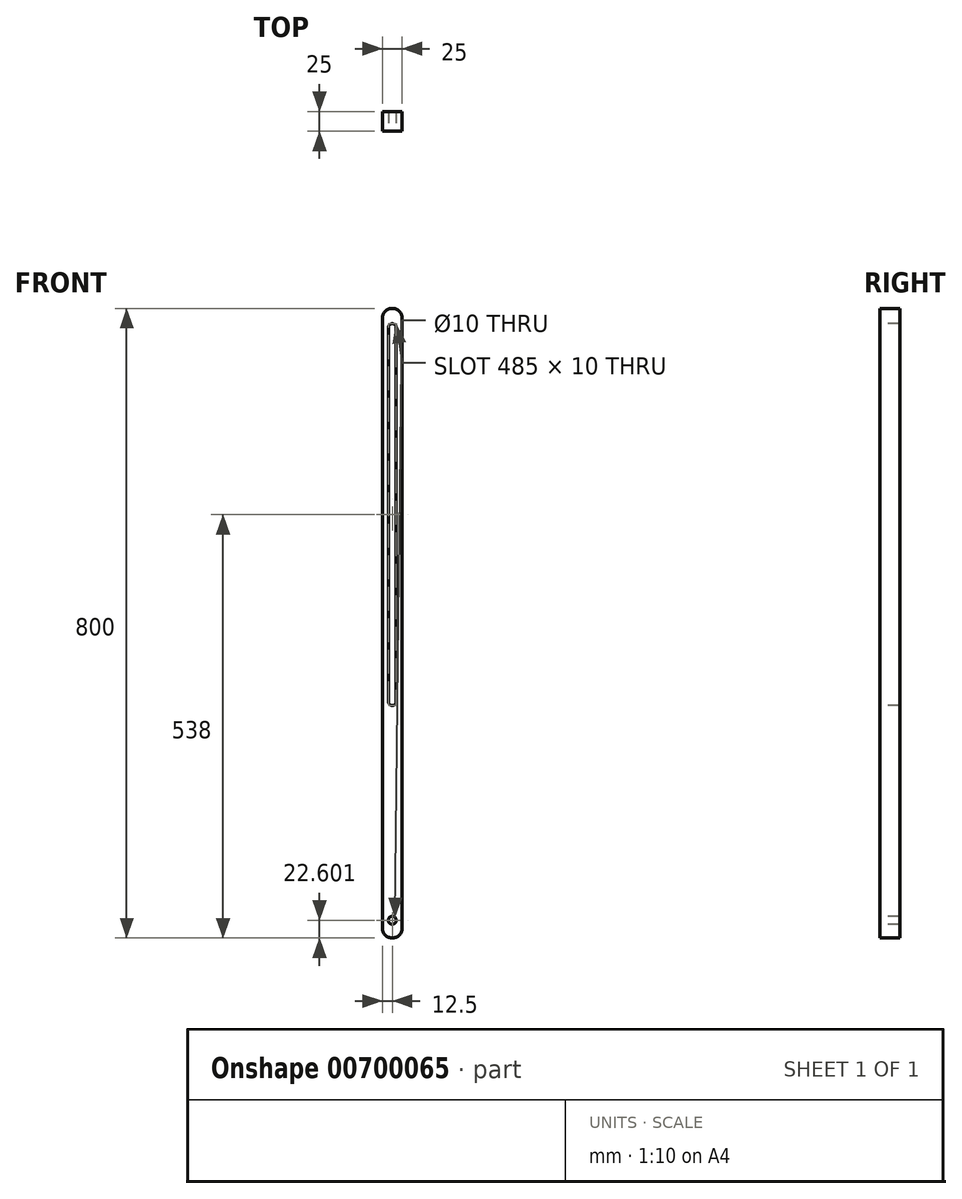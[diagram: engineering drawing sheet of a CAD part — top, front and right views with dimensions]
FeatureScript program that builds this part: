
annotation { "Feature Type Name" : "Feature", "Feature Type Description" : "" }
export const myFeature = defineFeature(function(context is Context, id is Id, definition is map)
    precondition{}
    {
        {
            var Q0;
            Q0=qCreatedBy(makeId("Front.planeOp"),FACE);
            var sketch = newSketch(context, id + "F0", { "sketchPlane" : qUnion([Q0])});
            skLineSegment(sketch, "E0.bottom", {"start": v(-12.5, 400) * mm, "end": v(12.5, 400) * mm});
            skLineSegment(sketch, "E0.top", {"start": v(-12.5, -400) * mm, "end": v(12.5, -400) * mm});
            skLineSegment(sketch, "E0.left", {"start": v(-12.5, 400) * mm, "end": v(-12.5, -400) * mm});
            skLineSegment(sketch, "E0.right", {"start": v(12.5, 400) * mm, "end": v(12.5, -400) * mm});
            skPoint(sketch, "E0.middle", {"position": v(0, 0) * mm});
            skSolve(sketch);
        }
        {
            var Q0;
            Q0=makeQuery(id+"F0.imprint","IMPRINT",FACE,{"disambiguationData":[TD([[makeQuery(id+"F0.imprint","IMPRINT",EDGE,{"derivedFrom":sQuery(id+"F0.wireOp",EDGE,"E0.bottom")}),-1.0]])]});
            extrude(context, id + "F1", {"entities" : qUnion([Q0]), "depth" : 25 * mm, "offsetDistance" : 25.4 * mm});
        }
        {
            var Q0;
            Q0=makeQuery(id+"F1.opExtrude","CAP_FACE",FACE,{"disambiguationData":[OSD([sQuery(id+"F0.wireOp",EDGE,"E0.bottom"),sQuery(id+"F0.wireOp",EDGE,"E0.top"),sQuery(id+"F0.wireOp",EDGE,"E0.left"),sQuery(id+"F0.wireOp",EDGE,"E0.right")])],"isStart":false});
            var sketch = newSketch(context, id + "F2", { "sketchPlane" : qUnion([Q0])});
            skLineSegment(sketch, "E1.bottom", {"start": v(5, 375.5) * mm, "end": v(-5, 375.5) * mm});
            skLineSegment(sketch, "E1.top", {"start": v(5, -99.5) * mm, "end": v(-5, -99.5) * mm});
            skLineSegment(sketch, "E1.left", {"start": v(5, 375.5) * mm, "end": v(5, -99.5) * mm});
            skLineSegment(sketch, "E1.right", {"start": v(-5, 375.5) * mm, "end": v(-5, -99.5) * mm});
            skPoint(sketch, "E1.middle", {"position": v(0, 138) * mm});
            skSolve(sketch);
        }
        {
            var Q0;
            Q0=makeQuery(id+"F2.imprint","IMPRINT",FACE,{"disambiguationData":[TD([[makeQuery(id+"F2.imprint","IMPRINT",EDGE,{"derivedFrom":sQuery(id+"F2.wireOp",EDGE,"E1.bottom")}),1.0]])]});
            extrude(context, id + "F3", {"entities" : qUnion([Q0]), "operationType" : NewBodyOperationType.REMOVE, "oppositeDirection" : true, "depth" : 25 * mm, "offsetDistance" : 25 * mm});
        }
        {
            var Q0;
            Q0=makeQuery(id+"F1.opExtrude","CAP_FACE",FACE,{"disambiguationData":[OSD([sQuery(id+"F0.wireOp",EDGE,"E0.bottom"),sQuery(id+"F0.wireOp",EDGE,"E0.top"),sQuery(id+"F0.wireOp",EDGE,"E0.left"),sQuery(id+"F0.wireOp",EDGE,"E0.right")])],"isStart":false});
            var sketch = newSketch(context, id + "F4", { "sketchPlane" : qUnion([Q0])});
            skCircle(sketch, "E2", {"center": v(0, -377.4) * mm, "radius": 5 * mm});
            skSolve(sketch);
        }
        {
            var Q0;
            Q0=makeQuery(id+"F4.imprint","IMPRINT",FACE,{"disambiguationData":[TD([[makeQuery(id+"F4.imprint","IMPRINT",EDGE,{"derivedFrom":sQuery(id+"F4.wireOp",EDGE,"E2")}),1.0]])]});
            extrude(context, id + "F5", {"entities" : qUnion([Q0]), "operationType" : NewBodyOperationType.REMOVE, "oppositeDirection" : true, "depth" : 25 * mm, "offsetDistance" : 25 * mm});
        }
        {
            var Q0;
            Q0=makeQuery(id+"F1.opExtrude","CAP_FACE",FACE,{"disambiguationData":[OSD([sQuery(id+"F0.wireOp",EDGE,"E0.bottom"),sQuery(id+"F0.wireOp",EDGE,"E0.top"),sQuery(id+"F0.wireOp",EDGE,"E0.left"),sQuery(id+"F0.wireOp",EDGE,"E0.right")])],"isStart":false});
            var sketch = newSketch(context, id + "F6", { "sketchPlane" : qUnion([Q0])});
            skArc(sketch, "E3", {"start": v(5, 375.5) * mm, "mid": v(0, 380.5) * mm, "end": v(-5, 375.5) * mm});
            skSolve(sketch);
        }
        {
            var Q0;
            Q0=makeQuery(id+"F6.imprint","IMPRINT",FACE,{"disambiguationData":[TD([[makeQuery(id+"F6.imprint","IMPRINT",EDGE,{"derivedFrom":sQuery(id+"F6.wireOp",EDGE,"E3")}),1.0]])]});
            extrude(context, id + "F7", {"entities" : qUnion([Q0]), "operationType" : NewBodyOperationType.REMOVE, "oppositeDirection" : true, "depth" : 25 * mm, "offsetDistance" : 25 * mm});
        }
        {
            var Q0;
            Q0=makeQuery(id+"F1.opExtrude","CAP_FACE",FACE,{"disambiguationData":[OSD([sQuery(id+"F0.wireOp",EDGE,"E0.bottom"),sQuery(id+"F0.wireOp",EDGE,"E0.top"),sQuery(id+"F0.wireOp",EDGE,"E0.left"),sQuery(id+"F0.wireOp",EDGE,"E0.right")])],"isStart":false});
            var sketch = newSketch(context, id + "F8", { "sketchPlane" : qUnion([Q0])});
            skArc(sketch, "E4", {"start": v(-5, -99.5) * mm, "mid": v(0, -104.5) * mm, "end": v(5, -99.5) * mm});
            skSolve(sketch);
        }
        {
            var Q0;
            Q0=makeQuery(id+"F8.imprint","IMPRINT",FACE,{"disambiguationData":[TD([[makeQuery(id+"F8.imprint","IMPRINT",EDGE,{"derivedFrom":sQuery(id+"F8.wireOp",EDGE,"E4")}),1.0]])]});
            extrude(context, id + "F9", {"entities" : qUnion([Q0]), "operationType" : NewBodyOperationType.REMOVE, "oppositeDirection" : true, "depth" : 25 * mm, "offsetDistance" : 25 * mm});
        }
        {
            var Q0;
            Q0=makeQuery(id+"F1.opExtrude","SWEPT_EDGE",EDGE,{"disambiguationData":[OSD([sQuery(id+"F0.wireOp",EDGE,"E0.bottom"),sQuery(id+"F0.wireOp",EDGE,"E0.left")])]});
            var Q1;
            Q1=makeQuery(id+"F1.opExtrude","SWEPT_EDGE",EDGE,{"disambiguationData":[OSD([sQuery(id+"F0.wireOp",EDGE,"E0.bottom"),sQuery(id+"F0.wireOp",EDGE,"E0.right")])]});
            fillet(context, id + "F10", {"entities" : qUnion([Q0, Q1]), "radius" : 12.5 * mm, "tangentPropagation" : true, "allowEdgeOverflow" : false});
        }
        {
            var Q0;
            Q0=makeQuery(id+"F1.opExtrude","SWEPT_EDGE",EDGE,{"disambiguationData":[OSD([sQuery(id+"F0.wireOp",EDGE,"E0.top"),sQuery(id+"F0.wireOp",EDGE,"E0.left")])]});
            var Q1;
            Q1=makeQuery(id+"F1.opExtrude","SWEPT_EDGE",EDGE,{"disambiguationData":[OSD([sQuery(id+"F0.wireOp",EDGE,"E0.top"),sQuery(id+"F0.wireOp",EDGE,"E0.right")])]});
            fillet(context, id + "F11", {"entities" : qUnion([Q0, Q1]), "radius" : 12.5 * mm, "tangentPropagation" : true, "allowEdgeOverflow" : false});
        }
    });
